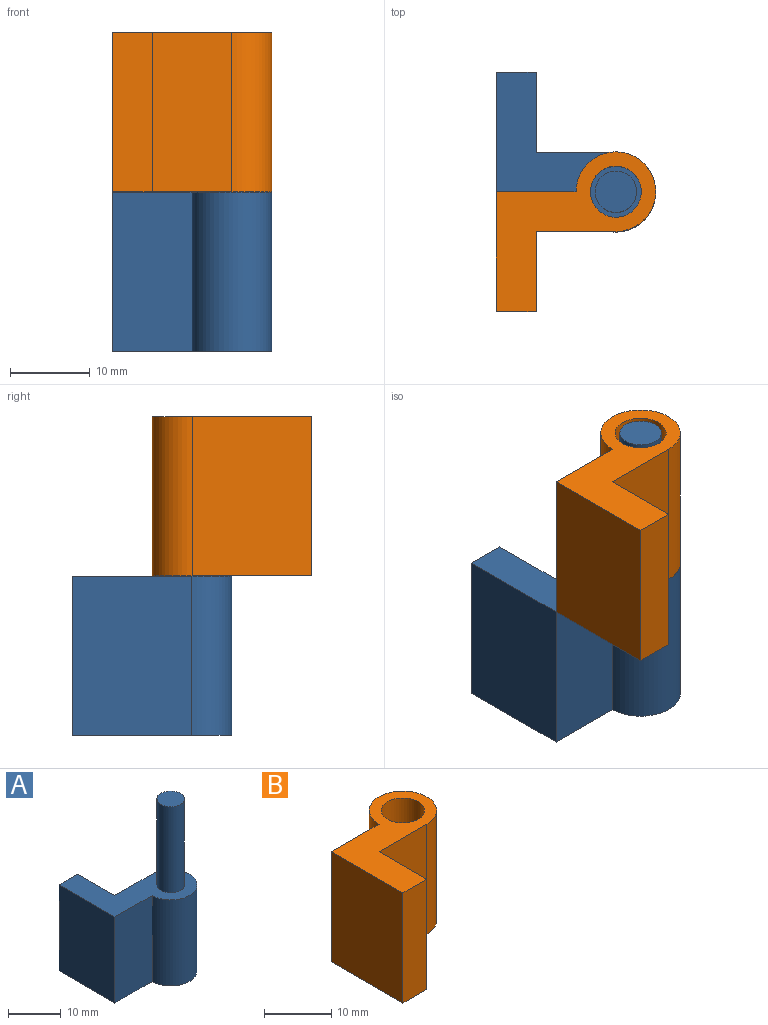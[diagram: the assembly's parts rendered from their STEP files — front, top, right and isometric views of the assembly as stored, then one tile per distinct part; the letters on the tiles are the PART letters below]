
ASSEMBLY  parts=2 mates=1
PART A: 10 faces, bbox 20x20x40 mm
  f0: plane 20x15mm, normal (-1,0,0), area 300mm2, adj f1,f5,f6,f7
  f1: plane 20x10mm, normal (0,-1,0), area 200mm2, adj f0,f2,f6,f7
  f2: cylinder r=5mm len=20mm, axis (0,0,-1), area 471.2mm2, adj f1,f3,f6,f7
  f3: plane 20x10mm, normal (0,1,0), area 200mm2, adj f2,f4,f6,f7
  f4: plane 20x10mm, normal (1,0,0), area 200mm2, adj f3,f5,f6,f7
  f5: plane 20x5mm, normal (0,1,0), area 100mm2, adj f0,f4,f6,f7
  f6: plane 20x20mm, normal (0,0,1), area 162.7mm2, adj f0,f1,f2,f3,f4,f5,f8
  f7: plane 20x20mm, normal (0,0,-1), area 183.9mm2, adj f0,f1,f2,f3,f4,f5
  f8: cylinder r=2.6mm len=20mm, axis (0,0,-1), area 326.7mm2, adj f6,f9
  f9: plane 5.2x5.2mm, normal (0,0,1), area 21.2mm2, adj f8
PART B: 9 faces, bbox 20x20x20 mm
  f0: plane 20x10mm, normal (0,1,0), area 200mm2, adj f1,f5,f7,f8
  f1: plane 20x15mm, normal (-1,0,0), area 300mm2, adj f0,f2,f7,f8
  f2: plane 20x5mm, normal (0,-1,0), area 100mm2, adj f1,f3,f7,f8
  f3: plane 20x10mm, normal (1,0,0), area 200mm2, adj f2,f4,f7,f8
  f4: plane 20x10mm, normal (0,-1,0), area 200mm2, adj f3,f5,f7,f8
  f5: cylinder r=5mm len=20mm, axis (0,0,-1), area 471.2mm2, adj f0,f4,f7,f8
  f6: cylinder r=3.2mm len=20mm, axis (0,0,-1), area 402.1mm2, adj f7,f8
  f7: plane 20x20mm, normal (0,0,1), area 151.7mm2, adj f0,f1,f2,f3,f4,f5,f6
  f8: plane 20x20mm, normal (0,0,-1), area 151.7mm2, adj f0,f1,f2,f3,f4,f5,f6
PLACE A at identity
PLACE B t=(0,22.49,20)mm
MATE revolute A.f8 <-> B.f5  axis (0,0,1) through (0,0,40)mm
